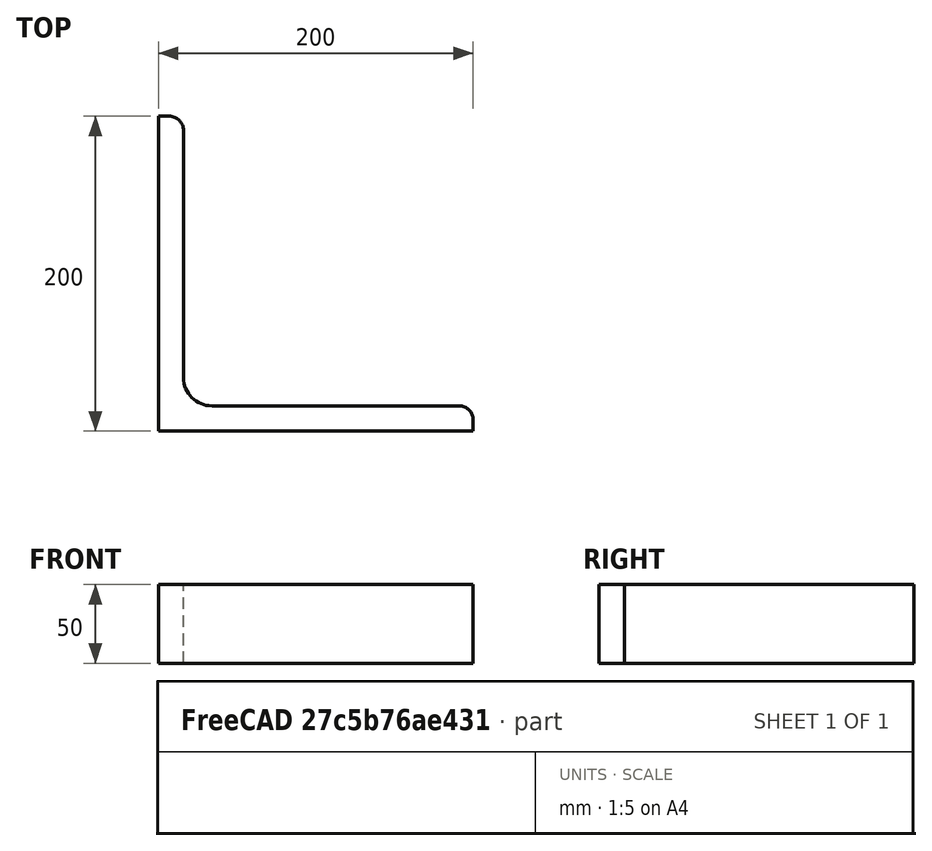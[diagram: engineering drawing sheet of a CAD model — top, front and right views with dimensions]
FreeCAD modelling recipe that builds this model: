
FCSTD DOCUMENT  (FreeCAD 0.15R4671 (Git))
Label: Angle Bar L200x200x16 EN10056 S235JR
License: All rights reserved
LicenseURL: http://en.wikipedia.org/wiki/All_rights_reserved
objects: Sketcher::SketchObject×1, Part::Extrusion×1
note: 2 computed .brp shape members not serialized (recipe doc carries the construction recipe); baked Part::Feature solids carry a one-line shape summary decoded from their .brp

FEATURE [Sketcher::SketchObject] Sketch
  sketch-geometry (9):
    g0: LineSegment StartX=0 StartY=0 StartZ=0 EndX=200 EndY=0 EndZ=0
    g1: LineSegment StartX=200 StartY=0 StartZ=0 EndX=200 EndY=7 EndZ=0
    g2: LineSegment StartX=191 StartY=16 StartZ=0 EndX=34 EndY=16 EndZ=0
    g3: LineSegment StartX=0 StartY=0 StartZ=0 EndX=0 EndY=200 EndZ=0
    g4: LineSegment StartX=0 StartY=200 StartZ=0 EndX=7 EndY=200 EndZ=0
    g5: LineSegment StartX=16 StartY=191 StartZ=0 EndX=16 EndY=34 EndZ=0
    g6: ArcOfCircle CenterX=34 CenterY=34 CenterZ=0 NormalX=0 NormalY=0 NormalZ=1 Radius=18 StartAngle=3.14159 EndAngle=4.71239
    g7: ArcOfCircle CenterX=7 CenterY=191 CenterZ=0 NormalX=0 NormalY=0 NormalZ=1 Radius=9 StartAngle=0 EndAngle=1.5708
    g8: ArcOfCircle CenterX=191 CenterY=7 CenterZ=0 NormalX=0 NormalY=0 NormalZ=1 Radius=9 StartAngle=0 EndAngle=1.5708
  constraints (23):
    c: Coincident(g0,g-1)
    c: Horizontal(g0)
    c: Coincident(g1,g0)
    c: Vertical(g1)
    c: Horizontal(g2)
    c: Coincident(g3,g-1)
    c: Vertical(g3)
    c: Coincident(g4,g3)
    c: Horizontal(g4)
    c: Vertical(g5)
    c: Tangent(g5,g6) = -1.5708
    c: Tangent(g2,g6) = 1.5708
    c: Tangent(g4,g7) = 1.5708
    c: Tangent(g5,g7) = 1.5708
    c: Tangent(g2,g8) = -1.5708
    c: Tangent(g1,g8) = -1.5708
    c: DistanceX(g0) = 200
    c: DistanceY(g3) = 200
    c: DistanceY(g0,g2) = 16
    c: DistanceX(g3,g5) = 16
    c: Radius(g6) = 18
    c: Radius(g8) = 9
    c: Radius(g7) = 9
FEATURE [Part::Extrusion] Extrude  label="Angle Bar L200x200x16 EN10056 S235JR"
  Base = -> Sketch
  Dir = (0,0,50)
  Solid = true
